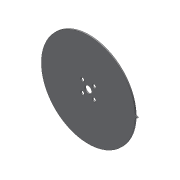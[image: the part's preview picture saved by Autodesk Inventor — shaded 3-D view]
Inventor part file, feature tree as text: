
AUTODESK INVENTOR PART (.ipt)
format: ipt  version: 2018 (Build 220112000, 112)  size: 110,080 bytes
history: native  units: mm
features: sketch x4, extrude x3, hole x1, projected_geometry x1
ambient origin geometry x8: Origin, YZ Plane, XZ Plane, XY Plane, X Axis, Y Axis, Z Axis, Center Point
bodies: Solid1 (feature_tree)
feature tree (9):
  extrude  "Extrusion1"  Depth=1.0mm
  extrude  "Extrusion2"  Depth=1.0mm TaperAngle=0.0deg
  hole  "Hole1"  [1 undecoded]
  extrude  "Extrusion3"  Depth=1.0mm
  sketch  "Sketch1"  dims[d0=1.0mm d1=0.0mm d2=80.0mm]
  sketch  "Sketch2"  dims[d3=6.0mm d4=1.0mm d5=0.0mm]
  sketch  "Sketch3"  dims[d6=14.0mm d7=14.0mm]
  sketch  "Sketch4"  dims[d8=9.899495mm d9=9.899495mm d10=3.2mm d11=6.35mm d12=6.3mm d13=2.0mm d14=90.0deg d15=9.525mm d16=20.594885mm d18=1.0mm d19=1.0mm d20=42.0mm d21=1.0mm d22=0.0mm]
  projected_geometry  "Projected Loop1"
note: 1 required parameter value undecoded (feature->parameter linkage not recoverable at this tier; creation-order binding heuristic only, values carry confidence <= 0.55)
